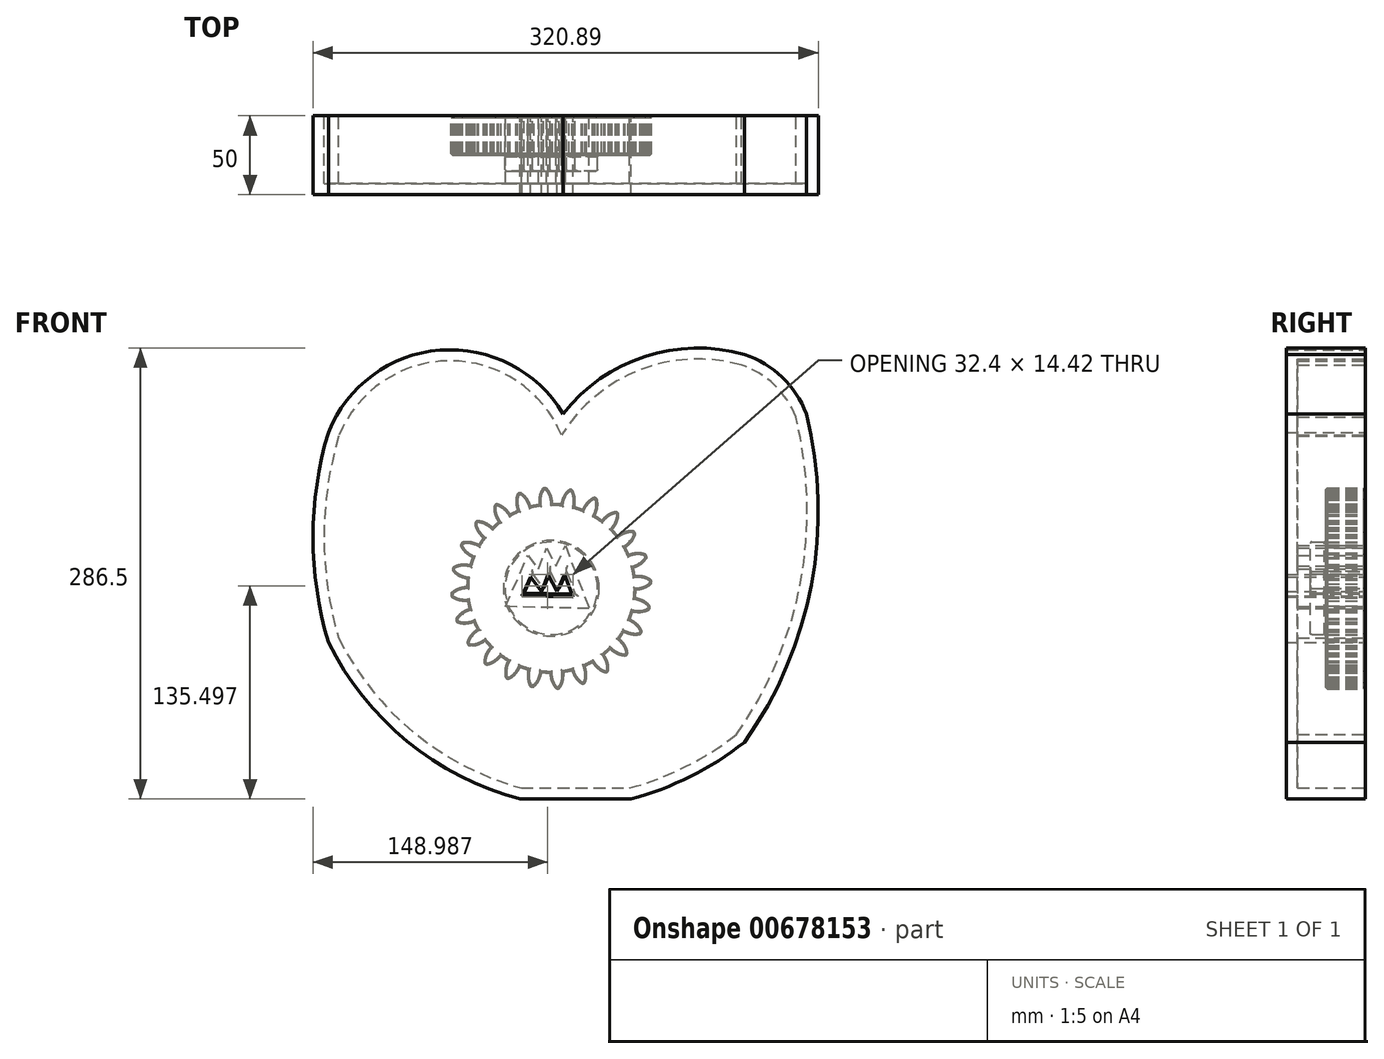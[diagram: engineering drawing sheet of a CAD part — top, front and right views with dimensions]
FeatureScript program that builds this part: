
annotation { "Feature Type Name" : "Feature", "Feature Type Description" : "" }
export const myFeature = defineFeature(function(context is Context, id is Id, definition is map)
    precondition{}
    {
        {
            var Q0;
            Q0=qCreatedBy(makeId("Front.planeOp"),FACE);
            var sketch = newSketch(context, id + "F0", { "sketchPlane" : qUnion([Q0])});
            skCircle(sketch, "E0", {"center": v(0, 0) * mm, "radius": 53.72 * mm});
            skCircle(sketch, "E1", {"center": v(0, 0) * mm, "radius": 58.67 * mm, "construction": true});
            skCircle(sketch, "E2", {"center": v(0, 0) * mm, "radius": 63.5 * mm, "construction": true});
            skLineSegment(sketch, "E3", {"start": v(0, 0) * mm, "end": v(0, 87.32) * mm, "construction": true});
            skLineSegment(sketch, "E4", {"start": v(0, 0) * mm, "end": v(-6.72, 102.52) * mm, "construction": true});
            skLineSegment(sketch, "E5", {"start": v(0, 58.67) * mm, "end": v(-57.61, 58.67) * mm, "construction": true});
            skLineSegment(sketch, "E6", {"start": v(0, 58.67) * mm, "end": v(-65.6, 34.8) * mm, "construction": true});
            skCircle(sketch, "E7", {"center": v(0, 0) * mm, "radius": 55.14 * mm, "construction": true});
            skCircle(sketch, "E8", {"center": v(0, 58.67) * mm, "radius": 14.6 * mm, "construction": true});
            skCircle(sketch, "E9", {"center": v(-13.72, 53.68) * mm, "radius": 14.6 * mm, "construction": true});
            skArc(sketch, "E10", {"start": v(0.88, 53.71) * mm, "mid": v(0.6, 56.22) * mm, "end": v(0, 58.67) * mm});
            skArc(sketch, "E11.MirrorCS", {"start": v(-7.66, 58.17) * mm, "mid": v(-6.86, 60.85) * mm, "end": v(-5.45, 63.27) * mm});
            skArc(sketch, "E12.MirrorCS", {"start": v(-7.88, 53.14) * mm, "mid": v(-7.93, 55.66) * mm, "end": v(-7.66, 58.17) * mm});
            skArc(sketch, "E13", {"start": v(0, 58.67) * mm, "mid": v(-1.18, 61.13) * mm, "end": v(-2.77, 63.34) * mm});
            skArc(sketch, "E14", {"start": v(-2.77, 63.34) * mm, "mid": v(-4.12, 63.8) * mm, "end": v(-5.45, 63.27) * mm});
            skCircle(sketch, "E15", {"center": v(0, 0) * mm, "radius": 29.38 * mm});
            skLineSegment(sketch, "E16", {"start": v(-17.22, -2.92) * mm, "end": v(-11.9, 9.15) * mm});
            skLineSegment(sketch, "E17", {"start": v(-11.9, 9.15) * mm, "end": v(-4.93, 0) * mm});
            skLineSegment(sketch, "E18", {"start": v(-4.93, 0) * mm, "end": v(-0.7, 10.8) * mm});
            skLineSegment(sketch, "E19", {"start": v(-0.7, 10.8) * mm, "end": v(5, 0) * mm});
            skLineSegment(sketch, "E20", {"start": v(5, 0) * mm, "end": v(9.74, 10.68) * mm});
            skLineSegment(sketch, "E21", {"start": v(9.74, 10.68) * mm, "end": v(15.18, -3.62) * mm});
            skLineSegment(sketch, "E22", {"start": v(15.18, -3.62) * mm, "end": v(-17.22, -2.92) * mm});
            skSolve(sketch);
        }
        {
            var Q0;
            {var subQ0=sQuery(id+"F0.wireOp",EDGE,"E0");var subQ1=makeQuery(id+"F0.imprint","INTERSECT",VERTEX,{"derivedFrom":[subQ0,sQuery(id+"F0.wireOp",EDGE,"E10")]});Q0=makeQuery(id+"F0.imprint","IMPRINT",FACE,{"disambiguationData":[TD([[makeQuery(id+"F0.imprint","IMPRINT",EDGE,{"disambiguationData":[TD([[subQ1,-1.0]])],"derivedFrom":subQ0}),1.0]])]});}
            var Q1;
            {var subQ1=sQuery(id+"F0.wireOp",EDGE,"E10");Q1=makeQuery(id+"F0.imprint","IMPRINT",FACE,{"disambiguationData":[TD([[makeQuery(id+"F0.imprint","IMPRINT",EDGE,{"derivedFrom":subQ1}),1.0]])]});}
            extrude(context, id + "F1", {"entities" : qUnion([Q0, Q1]), "depth" : 25 * mm, "offsetDistance" : 25 * mm});
        }
        {
            var Q0;
            Q0=makeQuery(id+"F1.opExtrude","SWEPT_BODY",BODY,{"disambiguationData":[OSD([sQuery(id+"F0.wireOp",EDGE,"E0"),sQuery(id+"F0.wireOp",EDGE,"E10"),sQuery(id+"F0.wireOp",EDGE,"E12.MirrorCS"),sQuery(id+"F0.wireOp",EDGE,"E11.MirrorCS"),sQuery(id+"F0.wireOp",EDGE,"E13"),sQuery(id+"F0.wireOp",EDGE,"E14")])]});
            var Q1;
            Q1=makeQuery(id+"F1.opExtrude","SWEPT_FACE",FACE,{"disambiguationData":[OSD([sQuery(id+"F0.wireOp",EDGE,"E0")])]});
            circularPattern(context, id + "F2", {"entities" : qUnion([Q0]), "axis" : qUnion([Q1]), "angle" : 360 * degree, "instanceCount" : 24, "equalSpace" : true});
        }
        {
            var Q0;
            Q0=makeQuery(id+"F0.imprint","IMPRINT",FACE,{"disambiguationData":[TD([[makeQuery(id+"F0.imprint","IMPRINT",EDGE,{"derivedFrom":sQuery(id+"F0.wireOp",EDGE,"E15")}),1.0]])]});
            extrude(context, id + "F3", {"entities" : qUnion([Q0]), "operationType" : NewBodyOperationType.ADD, "depth" : 35 * mm, "offsetDistance" : 25 * mm});
        }
        {
            var Q0;
            {var subQ0=makeQuery(id+"F1.opExtrude","CAP_FACE",FACE,{"disambiguationData":[OSD([sQuery(id+"F0.wireOp",EDGE,"E0"),sQuery(id+"F0.wireOp",EDGE,"E10"),sQuery(id+"F0.wireOp",EDGE,"E12.MirrorCS"),sQuery(id+"F0.wireOp",EDGE,"E11.MirrorCS"),sQuery(id+"F0.wireOp",EDGE,"E13"),sQuery(id+"F0.wireOp",EDGE,"E14"),sQuery(id+"F0.wireOp",EDGE,"E15")])],"isStart":false});Q0=makeQuery(id+"F3.boolean.opBoolean","MERGE",FACE,{"derivedFrom":[subQ0,makeQuery(id+"F2.opPattern","COPY",FACE,{"derivedFrom":subQ0,"instanceName":"1"}),makeQuery(id+"F2.opPattern","COPY",FACE,{"derivedFrom":subQ0,"instanceName":"2"}),makeQuery(id+"F2.opPattern","COPY",FACE,{"derivedFrom":subQ0,"instanceName":"3"}),makeQuery(id+"F2.opPattern","COPY",FACE,{"derivedFrom":subQ0,"instanceName":"4"}),makeQuery(id+"F2.opPattern","COPY",FACE,{"derivedFrom":subQ0,"instanceName":"5"}),makeQuery(id+"F2.opPattern","COPY",FACE,{"derivedFrom":subQ0,"instanceName":"6"}),makeQuery(id+"F2.opPattern","COPY",FACE,{"derivedFrom":subQ0,"instanceName":"7"}),makeQuery(id+"F2.opPattern","COPY",FACE,{"derivedFrom":subQ0,"instanceName":"8"}),makeQuery(id+"F2.opPattern","COPY",FACE,{"derivedFrom":subQ0,"instanceName":"9"}),makeQuery(id+"F2.opPattern","COPY",FACE,{"derivedFrom":subQ0,"instanceName":"10"}),makeQuery(id+"F2.opPattern","COPY",FACE,{"derivedFrom":subQ0,"instanceName":"11"}),makeQuery(id+"F2.opPattern","COPY",FACE,{"derivedFrom":subQ0,"instanceName":"12"}),makeQuery(id+"F2.opPattern","COPY",FACE,{"derivedFrom":subQ0,"instanceName":"13"}),makeQuery(id+"F2.opPattern","COPY",FACE,{"derivedFrom":subQ0,"instanceName":"14"}),makeQuery(id+"F2.opPattern","COPY",FACE,{"derivedFrom":subQ0,"instanceName":"15"}),makeQuery(id+"F2.opPattern","COPY",FACE,{"derivedFrom":subQ0,"instanceName":"16"}),makeQuery(id+"F2.opPattern","COPY",FACE,{"derivedFrom":subQ0,"instanceName":"17"}),makeQuery(id+"F2.opPattern","COPY",FACE,{"derivedFrom":subQ0,"instanceName":"18"}),makeQuery(id+"F2.opPattern","COPY",FACE,{"derivedFrom":subQ0,"instanceName":"19"}),makeQuery(id+"F2.opPattern","COPY",FACE,{"derivedFrom":subQ0,"instanceName":"20"}),makeQuery(id+"F2.opPattern","COPY",FACE,{"derivedFrom":subQ0,"instanceName":"21"}),makeQuery(id+"F2.opPattern","COPY",FACE,{"derivedFrom":subQ0,"instanceName":"22"}),makeQuery(id+"F2.opPattern","COPY",FACE,{"derivedFrom":subQ0,"instanceName":"23"})]});}
            chamfer(context, id + "F4", {"entities" : qUnion([Q0]), "width" : 1 * mm, "tangentPropagation" : true});
        }
        {
            var Q0;
            {var subQ0=sQuery(id+"F0.wireOp",EDGE,"E15");var subQ1=makeQuery(id+"F1.opExtrude","CAP_FACE",FACE,{"disambiguationData":[OSD([sQuery(id+"F0.wireOp",EDGE,"E0"),sQuery(id+"F0.wireOp",EDGE,"E10"),sQuery(id+"F0.wireOp",EDGE,"E12.MirrorCS"),sQuery(id+"F0.wireOp",EDGE,"E11.MirrorCS"),sQuery(id+"F0.wireOp",EDGE,"E13"),sQuery(id+"F0.wireOp",EDGE,"E14"),subQ0])],"isStart":true});Q0=makeQuery(id+"F3.boolean.opBoolean","MERGE",FACE,{"derivedFrom":[subQ1,makeQuery(id+"F2.opPattern","COPY",FACE,{"derivedFrom":subQ1,"instanceName":"1"}),makeQuery(id+"F2.opPattern","COPY",FACE,{"derivedFrom":subQ1,"instanceName":"2"}),makeQuery(id+"F2.opPattern","COPY",FACE,{"derivedFrom":subQ1,"instanceName":"3"}),makeQuery(id+"F2.opPattern","COPY",FACE,{"derivedFrom":subQ1,"instanceName":"4"}),makeQuery(id+"F2.opPattern","COPY",FACE,{"derivedFrom":subQ1,"instanceName":"5"}),makeQuery(id+"F2.opPattern","COPY",FACE,{"derivedFrom":subQ1,"instanceName":"6"}),makeQuery(id+"F2.opPattern","COPY",FACE,{"derivedFrom":subQ1,"instanceName":"7"}),makeQuery(id+"F2.opPattern","COPY",FACE,{"derivedFrom":subQ1,"instanceName":"8"}),makeQuery(id+"F2.opPattern","COPY",FACE,{"derivedFrom":subQ1,"instanceName":"9"}),makeQuery(id+"F2.opPattern","COPY",FACE,{"derivedFrom":subQ1,"instanceName":"10"}),makeQuery(id+"F2.opPattern","COPY",FACE,{"derivedFrom":subQ1,"instanceName":"11"}),makeQuery(id+"F2.opPattern","COPY",FACE,{"derivedFrom":subQ1,"instanceName":"12"}),makeQuery(id+"F2.opPattern","COPY",FACE,{"derivedFrom":subQ1,"instanceName":"13"}),makeQuery(id+"F2.opPattern","COPY",FACE,{"derivedFrom":subQ1,"instanceName":"14"}),makeQuery(id+"F2.opPattern","COPY",FACE,{"derivedFrom":subQ1,"instanceName":"15"}),makeQuery(id+"F2.opPattern","COPY",FACE,{"derivedFrom":subQ1,"instanceName":"16"}),makeQuery(id+"F2.opPattern","COPY",FACE,{"derivedFrom":subQ1,"instanceName":"17"}),makeQuery(id+"F2.opPattern","COPY",FACE,{"derivedFrom":subQ1,"instanceName":"18"}),makeQuery(id+"F2.opPattern","COPY",FACE,{"derivedFrom":subQ1,"instanceName":"19"}),makeQuery(id+"F2.opPattern","COPY",FACE,{"derivedFrom":subQ1,"instanceName":"20"}),makeQuery(id+"F2.opPattern","COPY",FACE,{"derivedFrom":subQ1,"instanceName":"21"}),makeQuery(id+"F2.opPattern","COPY",FACE,{"derivedFrom":subQ1,"instanceName":"22"}),makeQuery(id+"F2.opPattern","COPY",FACE,{"derivedFrom":subQ1,"instanceName":"23"}),makeQuery(id+"F3.opExtrude","CAP_FACE",FACE,{"disambiguationData":[OSD([subQ0,sQuery(id+"F0.wireOp",EDGE,"JNtdXsKn-sl94-sJaL-X6j9-ipqJ5UrsfOhM"),sQuery(id+"F0.wireOp",EDGE,"nhLlYziE-T9go-qMXb-Lngr-M2SgK2O0rp0T"),sQuery(id+"F0.wireOp",EDGE,"FmWoKXcW-Qzj9-4IRf-52Ky-pHPL5FFvMOR0"),sQuery(id+"F0.wireOp",EDGE,"DI1x3HvC-3bFb-MIyR-UmgX-l09uo7GKVcLs"),sQuery(id+"F0.wireOp",EDGE,"HNXKMdma-7YMK-hGZH-avgI-vMgkNqy3HRcJ"),sQuery(id+"F0.wireOp",EDGE,"5TuZqJqq-FCUH-1mfl-Rlqv-17RgC5mEEKbx"),sQuery(id+"F0.wireOp",EDGE,"hMIrZLfI-JfvP-B32Z-qgZj-gbDX4PTdaB8e")])],"isStart":true})]});}
            chamfer(context, id + "F5", {"entities" : qUnion([Q0]), "width" : mm, "tangentPropagation" : true});
        }
        {
            var Q0;
            Q0=makeQuery(id+"F3.opExtrude","CAP_FACE",FACE,{"disambiguationData":[OSD([sQuery(id+"F0.wireOp",EDGE,"E15"),sQuery(id+"F0.wireOp",EDGE,"JNtdXsKn-sl94-sJaL-X6j9-ipqJ5UrsfOhM"),sQuery(id+"F0.wireOp",EDGE,"nhLlYziE-T9go-qMXb-Lngr-M2SgK2O0rp0T"),sQuery(id+"F0.wireOp",EDGE,"FmWoKXcW-Qzj9-4IRf-52Ky-pHPL5FFvMOR0"),sQuery(id+"F0.wireOp",EDGE,"DI1x3HvC-3bFb-MIyR-UmgX-l09uo7GKVcLs"),sQuery(id+"F0.wireOp",EDGE,"HNXKMdma-7YMK-hGZH-avgI-vMgkNqy3HRcJ"),sQuery(id+"F0.wireOp",EDGE,"5TuZqJqq-FCUH-1mfl-Rlqv-17RgC5mEEKbx"),sQuery(id+"F0.wireOp",EDGE,"hMIrZLfI-JfvP-B32Z-qgZj-gbDX4PTdaB8e")])],"isStart":false});
            fillet(context, id + "F6", {"entities" : qUnion([Q0]), "radius" : 1 * mm, "tangentPropagation" : true, "allowEdgeOverflow" : false});
        }
        {
            var Q0;
            {var subQ0=sQuery(id+"F0.wireOp",EDGE,"E15");var subQ1=makeQuery(id+"F1.opExtrude","CAP_FACE",FACE,{"disambiguationData":[OSD([sQuery(id+"F0.wireOp",EDGE,"E0"),sQuery(id+"F0.wireOp",EDGE,"E10"),sQuery(id+"F0.wireOp",EDGE,"E12.MirrorCS"),sQuery(id+"F0.wireOp",EDGE,"E11.MirrorCS"),sQuery(id+"F0.wireOp",EDGE,"E13"),sQuery(id+"F0.wireOp",EDGE,"E14"),subQ0])],"isStart":true});Q0=makeQuery(id+"F3.boolean.opBoolean","MERGE",FACE,{"derivedFrom":[subQ1,makeQuery(id+"F2.opPattern","COPY",FACE,{"derivedFrom":subQ1,"instanceName":"1"}),makeQuery(id+"F2.opPattern","COPY",FACE,{"derivedFrom":subQ1,"instanceName":"2"}),makeQuery(id+"F2.opPattern","COPY",FACE,{"derivedFrom":subQ1,"instanceName":"3"}),makeQuery(id+"F2.opPattern","COPY",FACE,{"derivedFrom":subQ1,"instanceName":"4"}),makeQuery(id+"F2.opPattern","COPY",FACE,{"derivedFrom":subQ1,"instanceName":"5"}),makeQuery(id+"F2.opPattern","COPY",FACE,{"derivedFrom":subQ1,"instanceName":"6"}),makeQuery(id+"F2.opPattern","COPY",FACE,{"derivedFrom":subQ1,"instanceName":"7"}),makeQuery(id+"F2.opPattern","COPY",FACE,{"derivedFrom":subQ1,"instanceName":"8"}),makeQuery(id+"F2.opPattern","COPY",FACE,{"derivedFrom":subQ1,"instanceName":"9"}),makeQuery(id+"F2.opPattern","COPY",FACE,{"derivedFrom":subQ1,"instanceName":"10"}),makeQuery(id+"F2.opPattern","COPY",FACE,{"derivedFrom":subQ1,"instanceName":"11"}),makeQuery(id+"F2.opPattern","COPY",FACE,{"derivedFrom":subQ1,"instanceName":"12"}),makeQuery(id+"F2.opPattern","COPY",FACE,{"derivedFrom":subQ1,"instanceName":"13"}),makeQuery(id+"F2.opPattern","COPY",FACE,{"derivedFrom":subQ1,"instanceName":"14"}),makeQuery(id+"F2.opPattern","COPY",FACE,{"derivedFrom":subQ1,"instanceName":"15"}),makeQuery(id+"F2.opPattern","COPY",FACE,{"derivedFrom":subQ1,"instanceName":"16"}),makeQuery(id+"F2.opPattern","COPY",FACE,{"derivedFrom":subQ1,"instanceName":"17"}),makeQuery(id+"F2.opPattern","COPY",FACE,{"derivedFrom":subQ1,"instanceName":"18"}),makeQuery(id+"F2.opPattern","COPY",FACE,{"derivedFrom":subQ1,"instanceName":"19"}),makeQuery(id+"F2.opPattern","COPY",FACE,{"derivedFrom":subQ1,"instanceName":"20"}),makeQuery(id+"F2.opPattern","COPY",FACE,{"derivedFrom":subQ1,"instanceName":"21"}),makeQuery(id+"F2.opPattern","COPY",FACE,{"derivedFrom":subQ1,"instanceName":"22"}),makeQuery(id+"F2.opPattern","COPY",FACE,{"derivedFrom":subQ1,"instanceName":"23"}),makeQuery(id+"F3.opExtrude","CAP_FACE",FACE,{"disambiguationData":[OSD([subQ0,sQuery(id+"F0.wireOp",EDGE,"JNtdXsKn-sl94-sJaL-X6j9-ipqJ5UrsfOhM"),sQuery(id+"F0.wireOp",EDGE,"nhLlYziE-T9go-qMXb-Lngr-M2SgK2O0rp0T"),sQuery(id+"F0.wireOp",EDGE,"FmWoKXcW-Qzj9-4IRf-52Ky-pHPL5FFvMOR0"),sQuery(id+"F0.wireOp",EDGE,"DI1x3HvC-3bFb-MIyR-UmgX-l09uo7GKVcLs"),sQuery(id+"F0.wireOp",EDGE,"HNXKMdma-7YMK-hGZH-avgI-vMgkNqy3HRcJ"),sQuery(id+"F0.wireOp",EDGE,"5TuZqJqq-FCUH-1mfl-Rlqv-17RgC5mEEKbx"),sQuery(id+"F0.wireOp",EDGE,"hMIrZLfI-JfvP-B32Z-qgZj-gbDX4PTdaB8e")])],"isStart":true})]});}
            fillet(context, id + "F7", {"entities" : qUnion([Q0]), "radius" : 1 * mm, "tangentPropagation" : true, "allowEdgeOverflow" : false});
        }
        {
            var Q0;
            Q0=qCreatedBy(makeId("Front.planeOp"),FACE);
            var sketch = newSketch(context, id + "F8", { "sketchPlane" : qUnion([Q0])});
            skArc(sketch, "E23", {"start": v(7.45, 110.88) * mm, "mid": v(-70.73, 151.25) * mm, "end": v(-141.6, 99.12) * mm});
            skArc(sketch, "E24", {"start": v(-141.6, 99.12) * mm, "mid": v(-151.35, 32.44) * mm, "end": v(-141.6, -34.24) * mm});
            skArc(sketch, "E25", {"start": v(-141.6, -34.24) * mm, "mid": v(-91.5, -97.11) * mm, "end": v(-20, -133.87) * mm});
            skArc(sketch, "E26", {"start": v(122.76, 148.54) * mm, "mid": v(59.38, 147.25) * mm, "end": v(7.45, 110.88) * mm});
            skArc(sketch, "E27", {"start": v(161.99, 110.88) * mm, "mid": v(146.6, 134.12) * mm, "end": v(122.76, 148.54) * mm});
            skArc(sketch, "E28", {"start": v(122.76, -97.78) * mm, "mid": v(165.16, 2.27) * mm, "end": v(161.99, 110.88) * mm});
            skArc(sketch, "E29", {"start": v(50.6, -133.87) * mm, "mid": v(88.48, -119.44) * mm, "end": v(122.76, -97.78) * mm});
            skLineSegment(sketch, "E30", {"start": v(-20, -133.87) * mm, "end": v(50.6, -133.87) * mm});
            skLineSegment(sketch, "E31", {"start": v(-18.56, -4.88) * mm, "end": v(-13.24, 7.19) * mm});
            skLineSegment(sketch, "E32", {"start": v(-13.24, 7.19) * mm, "end": v(-6.27, -1.96) * mm});
            skLineSegment(sketch, "E33", {"start": v(-6.27, -1.96) * mm, "end": v(-2.05, 8.84) * mm});
            skLineSegment(sketch, "E34", {"start": v(-2.05, 8.84) * mm, "end": v(3.67, -1.96) * mm});
            skLineSegment(sketch, "E35", {"start": v(3.67, -1.96) * mm, "end": v(8.4, 8.72) * mm});
            skLineSegment(sketch, "E36", {"start": v(8.4, 8.72) * mm, "end": v(13.84, -5.59) * mm});
            skLineSegment(sketch, "E37", {"start": v(13.84, -5.59) * mm, "end": v(-18.56, -4.88) * mm});
            skSolve(sketch);
        }
        {
            var Q0;
            Q0=makeQuery(id+"F8.imprint","IMPRINT",FACE,{"disambiguationData":[TD([[makeQuery(id+"F8.imprint","IMPRINT",EDGE,{"derivedFrom":sQuery(id+"F8.wireOp",EDGE,"E23")}),1.0]])]});
            extrude(context, id + "F9", {"entities" : qUnion([Q0]), "depth" : 50 * mm, "offsetDistance" : 25 * mm});
        }
        {
            var Q0;
            Q0=makeQuery(id+"F9.opExtrude","CAP_FACE",FACE,{"disambiguationData":[OSD([sQuery(id+"F8.wireOp",EDGE,"E23"),sQuery(id+"F8.wireOp",EDGE,"E24"),sQuery(id+"F8.wireOp",EDGE,"E25"),sQuery(id+"F8.wireOp",EDGE,"E26"),sQuery(id+"F8.wireOp",EDGE,"E27"),sQuery(id+"F8.wireOp",EDGE,"E28"),sQuery(id+"F8.wireOp",EDGE,"E29"),sQuery(id+"F8.wireOp",EDGE,"E30")])],"isStart":true});
            shell(context, id + "F10", {"entities" : qUnion([Q0]), "thickness" : 7 * mm});
        }
    });
